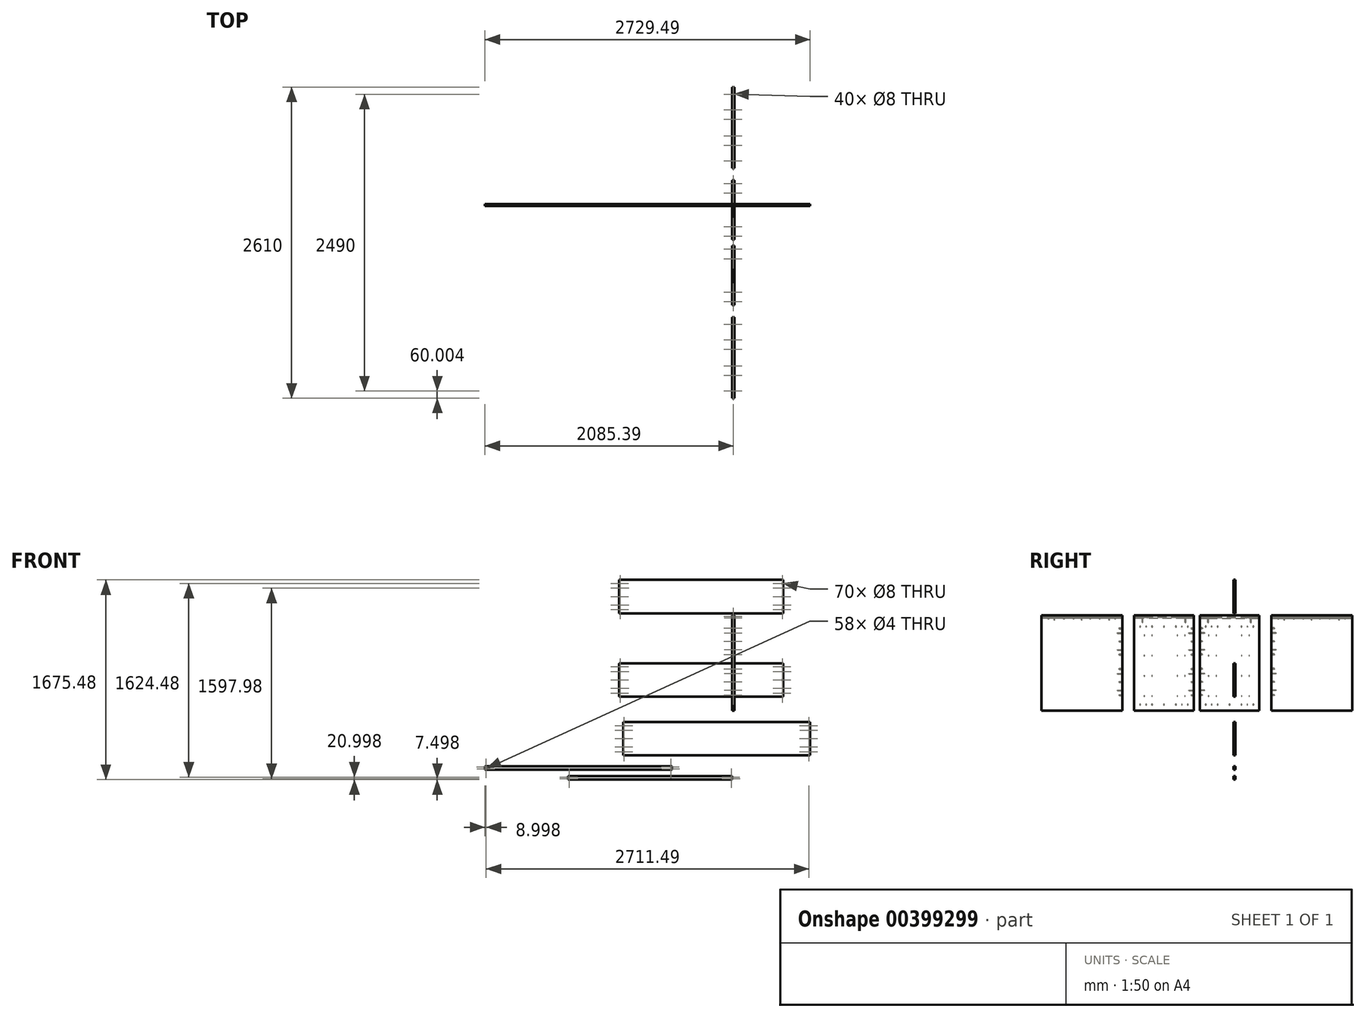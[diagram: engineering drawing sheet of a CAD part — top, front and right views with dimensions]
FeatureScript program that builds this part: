
annotation { "Feature Type Name" : "Feature", "Feature Type Description" : "" }
export const myFeature = defineFeature(function(context is Context, id is Id, definition is map)
    precondition{}
    {
        {
            var Q0;
            Q0=qCreatedBy(makeId("Right.planeOp"),FACE);
            var sketch = newSketch(context, id + "F0", { "sketchPlane" : qUnion([Q0])});
            skLineSegment(sketch, "E0.bottom", {"start": v(-300.67, 487.5) * mm, "end": v(199.33, 487.5) * mm});
            skLineSegment(sketch, "E0.top", {"start": v(-300.67, -312.5) * mm, "end": v(199.33, -312.5) * mm});
            skLineSegment(sketch, "E0.left", {"start": v(-300.67, 487.5) * mm, "end": v(-300.67, -312.5) * mm});
            skLineSegment(sketch, "E0.right", {"start": v(199.33, 487.5) * mm, "end": v(199.33, -312.5) * mm});
            skSolve(sketch);
        }
        {
            var Q0;
            Q0=makeQuery(id+"F0.imprint","IMPRINT",FACE,{"disambiguationData":[TD([[makeQuery(id+"F0.imprint","IMPRINT",EDGE,{"derivedFrom":sQuery(id+"F0.wireOp",EDGE,"E0.bottom")}),-1.0]])]});
            var sketch = newSketch(context, id + "F1", { "sketchPlane" : qUnion([Q0])});
            skLineSegment(sketch, "E1", {"start": v(-300.67, -262.5) * mm, "end": v(199.33, -262.5) * mm, "construction": true});
            skPoint(sketch, "E2", {"position": v(-250.67, -262.5) * mm});
            skPoint(sketch, "E3.1.0.0", {"position": v(-150.67, -262.5) * mm});
            skPoint(sketch, "E3.2.0.0", {"position": v(-50.67, -262.5) * mm});
            skPoint(sketch, "E3.3.0.0", {"position": v(49.33, -262.5) * mm});
            skPoint(sketch, "E3.4.0.0", {"position": v(149.33, -262.5) * mm});
            skLineSegment(sketch, "E3.direction1", {"start": v(-250.67, -262.5) * mm, "end": v(-150.67, -262.5) * mm, "construction": true});
            skPoint(sketch, "E4", {"position": v(99.33, -262.5) * mm});
            skPoint(sketch, "E5", {"position": v(-200.67, -262.5) * mm});
            skPoint(sketch, "E6.0.1.0", {"position": v(99.33, 392.5) * mm});
            skPoint(sketch, "E6.0.1.1", {"position": v(-150.67, 392.5) * mm});
            skPoint(sketch, "E6.0.1.2", {"position": v(-250.67, 392.5) * mm});
            skLineSegment(sketch, "E6.0.1.3", {"start": v(-300.67, 392.5) * mm, "end": v(199.33, 392.5) * mm, "construction": true});
            skPoint(sketch, "E6.0.1.4", {"position": v(-50.67, 392.5) * mm});
            skPoint(sketch, "E6.0.1.5", {"position": v(149.33, 392.5) * mm});
            skPoint(sketch, "E6.0.1.6", {"position": v(-200.67, 392.5) * mm});
            skPoint(sketch, "E6.0.1.7", {"position": v(49.33, 392.5) * mm});
            skLineSegment(sketch, "E6.0.1.8", {"start": v(-250.67, 392.5) * mm, "end": v(-150.67, 392.5) * mm, "construction": true});
            skPoint(sketch, "E6.1.0.0", {"position": v(124.33, -262.5) * mm});
            skPoint(sketch, "E6.1.0.1", {"position": v(-125.67, -262.5) * mm});
            skPoint(sketch, "E6.1.0.2", {"position": v(-225.67, -262.5) * mm});
            skLineSegment(sketch, "E6.1.0.3", {"start": v(-275.67, -262.5) * mm, "end": v(224.33, -262.5) * mm, "construction": true});
            skPoint(sketch, "E6.1.0.4", {"position": v(-25.67, -262.5) * mm});
            skPoint(sketch, "E6.1.0.5", {"position": v(174.33, -262.5) * mm});
            skPoint(sketch, "E6.1.0.6", {"position": v(-175.67, -262.5) * mm});
            skPoint(sketch, "E6.1.0.7", {"position": v(74.33, -262.5) * mm});
            skLineSegment(sketch, "E6.1.0.8", {"start": v(-225.67, -262.5) * mm, "end": v(-125.67, -262.5) * mm, "construction": true});
            skPoint(sketch, "E6.1.1.0", {"position": v(124.33, 392.5) * mm});
            skPoint(sketch, "E6.1.1.1", {"position": v(-125.67, 392.5) * mm});
            skPoint(sketch, "E6.1.1.2", {"position": v(-225.67, 392.5) * mm});
            skLineSegment(sketch, "E6.1.1.3", {"start": v(-275.67, 392.5) * mm, "end": v(224.33, 392.5) * mm, "construction": true});
            skPoint(sketch, "E6.1.1.4", {"position": v(-25.67, 392.5) * mm});
            skPoint(sketch, "E6.1.1.5", {"position": v(174.33, 392.5) * mm});
            skPoint(sketch, "E6.1.1.6", {"position": v(-175.67, 392.5) * mm});
            skPoint(sketch, "E6.1.1.7", {"position": v(74.33, 392.5) * mm});
            skLineSegment(sketch, "E6.1.1.8", {"start": v(-225.67, 392.5) * mm, "end": v(-125.67, 392.5) * mm, "construction": true});
            skPoint(sketch, "E6.2.0.1", {"position": v(-100.67, -262.5) * mm});
            skLineSegment(sketch, "E6.2.0.3", {"start": v(-250.67, -262.5) * mm, "end": v(249.33, -262.5) * mm, "construction": true});
            skPoint(sketch, "E6.2.0.4", {"position": v(-0.67, -262.5) * mm});
            skPoint(sketch, "E6.2.0.5", {"position": v(199.33, -262.5) * mm});
            skLineSegment(sketch, "E6.2.0.8", {"start": v(-200.67, -262.5) * mm, "end": v(-100.67, -262.5) * mm, "construction": true});
            skPoint(sketch, "E6.2.1.0", {"position": v(149.33, 392.5) * mm});
            skPoint(sketch, "E6.2.1.1", {"position": v(-100.67, 392.5) * mm});
            skPoint(sketch, "E6.2.1.2", {"position": v(-200.67, 392.5) * mm});
            skLineSegment(sketch, "E6.2.1.3", {"start": v(-250.67, 392.5) * mm, "end": v(249.33, 392.5) * mm, "construction": true});
            skPoint(sketch, "E6.2.1.4", {"position": v(-0.67, 392.5) * mm});
            skPoint(sketch, "E6.2.1.5", {"position": v(199.33, 392.5) * mm});
            skPoint(sketch, "E6.2.1.6", {"position": v(-150.67, 392.5) * mm});
            skPoint(sketch, "E6.2.1.7", {"position": v(99.33, 392.5) * mm});
            skLineSegment(sketch, "E6.2.1.8", {"start": v(-200.67, 392.5) * mm, "end": v(-100.67, 392.5) * mm, "construction": true});
            skLineSegment(sketch, "E6.direction1", {"start": v(-300.67, -262.5) * mm, "end": v(-275.67, -262.5) * mm, "construction": true});
            skLineSegment(sketch, "E6.direction2", {"start": v(-300.67, -262.5) * mm, "end": v(-300.67, 392.5) * mm, "construction": true});
            skSolve(sketch);
        }
        {
            var Q0;
            Q0=makeQuery(id+"F0.imprint","IMPRINT",FACE,{"disambiguationData":[TD([[makeQuery(id+"F0.imprint","IMPRINT",EDGE,{"derivedFrom":sQuery(id+"F0.wireOp",EDGE,"E0.bottom")}),-1.0]])]});
            var sketch = newSketch(context, id + "F2", { "sketchPlane" : qUnion([Q0])});
            skLineSegment(sketch, "E7.bottom", {"start": v(-263.67, -174.1) * mm, "end": v(186.33, -174.1) * mm});
            skLineSegment(sketch, "E7.top", {"start": v(-263.67, -208.9) * mm, "end": v(186.33, -208.9) * mm});
            skLineSegment(sketch, "E7.left", {"start": v(-263.67, -174.1) * mm, "end": v(-263.67, -208.9) * mm});
            skLineSegment(sketch, "E7.right", {"start": v(186.33, -174.1) * mm, "end": v(186.33, -208.9) * mm});
            skLineSegment(sketch, "E8", {"start": v(186.33, -191.5) * mm, "end": v(-263.67, -191.5) * mm, "construction": true});
            skCircle(sketch, "E9", {"center": v(114.63, -191.5) * mm, "radius": 2.5 * mm});
            skCircle(sketch, "E10", {"center": v(-226.42, -191.5) * mm, "radius": 2.5 * mm});
            skCircle(sketch, "E11", {"center": v(-162.42, -191.5) * mm, "radius": 2.5 * mm});
            skCircle(sketch, "E12", {"center": v(50.63, -191.5) * mm, "radius": 2.5 * mm});
            skCircle(sketch, "E13", {"center": v(-243.67, -191.5) * mm, "radius": 2.25 * mm});
            skLineSegment(sketch, "E14.bottom", {"start": v(134.63, -189.2) * mm, "end": v(125.23, -189.2) * mm});
            skLineSegment(sketch, "E14.top", {"start": v(134.63, -193.8) * mm, "end": v(125.23, -193.8) * mm});
            skLineSegment(sketch, "E14.left", {"start": v(134.63, -189.2) * mm, "end": v(134.63, -193.8) * mm});
            skLineSegment(sketch, "E14.right", {"start": v(125.23, -189.2) * mm, "end": v(125.23, -193.8) * mm});
            skPoint(sketch, "E14.middle", {"position": v(129.93, -191.5) * mm});
            skLineSegment(sketch, "E15.bottom", {"start": v(159.33, -189.2) * mm, "end": v(149.93, -189.2) * mm});
            skLineSegment(sketch, "E15.top", {"start": v(159.33, -193.8) * mm, "end": v(149.93, -193.8) * mm});
            skLineSegment(sketch, "E15.left", {"start": v(159.33, -189.2) * mm, "end": v(159.33, -193.8) * mm});
            skLineSegment(sketch, "E15.right", {"start": v(149.93, -189.2) * mm, "end": v(149.93, -193.8) * mm});
            skPoint(sketch, "E15.middle", {"position": v(154.63, -191.5) * mm});
            skLineSegment(sketch, "E16.bottom", {"start": v(70.63, -189.2) * mm, "end": v(61.23, -189.2) * mm});
            skLineSegment(sketch, "E16.top", {"start": v(70.63, -193.8) * mm, "end": v(61.23, -193.8) * mm});
            skLineSegment(sketch, "E16.left", {"start": v(70.63, -189.2) * mm, "end": v(70.63, -193.8) * mm});
            skLineSegment(sketch, "E16.right", {"start": v(61.23, -189.2) * mm, "end": v(61.23, -193.8) * mm});
            skPoint(sketch, "E16.middle", {"position": v(65.93, -191.5) * mm});
            skLineSegment(sketch, "E17.bottom", {"start": v(96.43, -189.2) * mm, "end": v(87.03, -189.2) * mm});
            skLineSegment(sketch, "E17.top", {"start": v(96.43, -193.8) * mm, "end": v(87.03, -193.8) * mm});
            skLineSegment(sketch, "E17.left", {"start": v(96.43, -189.2) * mm, "end": v(96.43, -193.8) * mm});
            skLineSegment(sketch, "E17.right", {"start": v(87.03, -189.2) * mm, "end": v(87.03, -193.8) * mm});
            skPoint(sketch, "E17.middle", {"position": v(91.73, -191.5) * mm});
            skLineSegment(sketch, "E18.bottom", {"start": v(-142.42, -189.2) * mm, "end": v(-151.82, -189.2) * mm});
            skLineSegment(sketch, "E18.top", {"start": v(-142.42, -193.8) * mm, "end": v(-151.82, -193.8) * mm});
            skLineSegment(sketch, "E18.left", {"start": v(-142.42, -189.2) * mm, "end": v(-142.42, -193.8) * mm});
            skLineSegment(sketch, "E18.right", {"start": v(-151.82, -189.2) * mm, "end": v(-151.82, -193.8) * mm});
            skPoint(sketch, "E18.middle", {"position": v(-147.12, -191.5) * mm});
            skLineSegment(sketch, "E19.bottom", {"start": v(-117.72, -189.2) * mm, "end": v(-127.12, -189.2) * mm});
            skLineSegment(sketch, "E19.top", {"start": v(-117.72, -193.8) * mm, "end": v(-127.12, -193.8) * mm});
            skLineSegment(sketch, "E19.left", {"start": v(-117.72, -189.2) * mm, "end": v(-117.72, -193.8) * mm});
            skLineSegment(sketch, "E19.right", {"start": v(-127.12, -189.2) * mm, "end": v(-127.12, -193.8) * mm});
            skPoint(sketch, "E19.middle", {"position": v(-122.42, -191.5) * mm});
            skLineSegment(sketch, "E20.bottom", {"start": v(-206.42, -189.2) * mm, "end": v(-215.82, -189.2) * mm});
            skLineSegment(sketch, "E20.top", {"start": v(-206.42, -193.8) * mm, "end": v(-215.82, -193.8) * mm});
            skLineSegment(sketch, "E20.left", {"start": v(-206.42, -189.2) * mm, "end": v(-206.42, -193.8) * mm});
            skLineSegment(sketch, "E20.right", {"start": v(-215.82, -189.2) * mm, "end": v(-215.82, -193.8) * mm});
            skPoint(sketch, "E20.middle", {"position": v(-211.12, -191.5) * mm});
            skLineSegment(sketch, "E21.bottom", {"start": v(-180.62, -189.2) * mm, "end": v(-190.02, -189.2) * mm});
            skLineSegment(sketch, "E21.top", {"start": v(-180.62, -193.8) * mm, "end": v(-190.02, -193.8) * mm});
            skLineSegment(sketch, "E21.left", {"start": v(-180.62, -189.2) * mm, "end": v(-180.62, -193.8) * mm});
            skLineSegment(sketch, "E21.right", {"start": v(-190.02, -189.2) * mm, "end": v(-190.02, -193.8) * mm});
            skPoint(sketch, "E21.middle", {"position": v(-185.32, -191.5) * mm});
            skLineSegment(sketch, "E22.0.1.0", {"start": v(186.33, -4.1) * mm, "end": v(186.33, -38.9) * mm});
            skPoint(sketch, "E22.0.1.1", {"position": v(-147.12, -21.5) * mm});
            skPoint(sketch, "E22.0.1.2", {"position": v(91.73, -21.5) * mm});
            skLineSegment(sketch, "E22.0.1.3", {"start": v(186.33, -21.5) * mm, "end": v(-263.67, -21.5) * mm, "construction": true});
            skPoint(sketch, "E22.0.1.4", {"position": v(-211.12, -21.5) * mm});
            skPoint(sketch, "E22.0.1.5", {"position": v(-185.32, -21.5) * mm});
            skLineSegment(sketch, "E22.0.1.6", {"start": v(-263.67, -4.1) * mm, "end": v(-263.67, -38.9) * mm});
            skLineSegment(sketch, "E22.0.1.7", {"start": v(-263.67, -4.1) * mm, "end": v(186.33, -4.1) * mm});
            skPoint(sketch, "E22.0.1.8", {"position": v(-122.42, -21.5) * mm});
            skPoint(sketch, "E22.0.1.9", {"position": v(154.63, -21.5) * mm});
            skPoint(sketch, "E22.0.1.10", {"position": v(129.93, -21.5) * mm});
            skLineSegment(sketch, "E22.0.1.11", {"start": v(-263.67, -38.9) * mm, "end": v(186.33, -38.9) * mm});
            skPoint(sketch, "E22.0.1.12", {"position": v(65.93, -21.5) * mm});
            skCircle(sketch, "E22.0.1.13", {"center": v(114.63, -21.5) * mm, "radius": 2.5 * mm});
            skCircle(sketch, "E22.0.1.14", {"center": v(-162.42, -21.5) * mm, "radius": 2.5 * mm});
            skCircle(sketch, "E22.0.1.15", {"center": v(-243.67, -21.5) * mm, "radius": 2.25 * mm});
            skCircle(sketch, "E22.0.1.16", {"center": v(-226.42, -21.5) * mm, "radius": 2.5 * mm});
            skCircle(sketch, "E22.0.1.17", {"center": v(50.63, -21.5) * mm, "radius": 2.5 * mm});
            skLineSegment(sketch, "E22.0.1.18", {"start": v(96.43, -19.2) * mm, "end": v(96.43, -23.8) * mm});
            skLineSegment(sketch, "E22.0.1.19", {"start": v(159.33, -19.2) * mm, "end": v(159.33, -23.8) * mm});
            skLineSegment(sketch, "E22.0.1.20", {"start": v(96.43, -23.8) * mm, "end": v(87.03, -23.8) * mm});
            skLineSegment(sketch, "E22.0.1.21", {"start": v(-180.62, -19.2) * mm, "end": v(-180.62, -23.8) * mm});
            skLineSegment(sketch, "E22.0.1.22", {"start": v(-117.72, -19.2) * mm, "end": v(-117.72, -23.8) * mm});
            skLineSegment(sketch, "E22.0.1.23", {"start": v(134.63, -23.8) * mm, "end": v(125.23, -23.8) * mm});
            skLineSegment(sketch, "E22.0.1.24", {"start": v(134.63, -19.2) * mm, "end": v(125.23, -19.2) * mm});
            skLineSegment(sketch, "E22.0.1.25", {"start": v(87.03, -19.2) * mm, "end": v(87.03, -23.8) * mm});
            skLineSegment(sketch, "E22.0.1.26", {"start": v(149.93, -19.2) * mm, "end": v(149.93, -23.8) * mm});
            skLineSegment(sketch, "E22.0.1.27", {"start": v(125.23, -19.2) * mm, "end": v(125.23, -23.8) * mm});
            skLineSegment(sketch, "E22.0.1.28", {"start": v(96.43, -19.2) * mm, "end": v(87.03, -19.2) * mm});
            skLineSegment(sketch, "E22.0.1.29", {"start": v(159.33, -23.8) * mm, "end": v(149.93, -23.8) * mm});
            skLineSegment(sketch, "E22.0.1.30", {"start": v(-190.02, -19.2) * mm, "end": v(-190.02, -23.8) * mm});
            skLineSegment(sketch, "E22.0.1.31", {"start": v(-180.62, -23.8) * mm, "end": v(-190.02, -23.8) * mm});
            skLineSegment(sketch, "E22.0.1.32", {"start": v(-151.82, -19.2) * mm, "end": v(-151.82, -23.8) * mm});
            skLineSegment(sketch, "E22.0.1.33", {"start": v(-180.62, -19.2) * mm, "end": v(-190.02, -19.2) * mm});
            skLineSegment(sketch, "E22.0.1.34", {"start": v(159.33, -19.2) * mm, "end": v(149.93, -19.2) * mm});
            skLineSegment(sketch, "E22.0.1.35", {"start": v(134.63, -19.2) * mm, "end": v(134.63, -23.8) * mm});
            skLineSegment(sketch, "E22.0.1.36", {"start": v(-142.42, -23.8) * mm, "end": v(-151.82, -23.8) * mm});
            skLineSegment(sketch, "E22.0.1.37", {"start": v(70.63, -19.2) * mm, "end": v(70.63, -23.8) * mm});
            skLineSegment(sketch, "E22.0.1.38", {"start": v(-142.42, -19.2) * mm, "end": v(-151.82, -19.2) * mm});
            skLineSegment(sketch, "E22.0.1.39", {"start": v(-117.72, -23.8) * mm, "end": v(-127.12, -23.8) * mm});
            skLineSegment(sketch, "E22.0.1.40", {"start": v(70.63, -23.8) * mm, "end": v(61.23, -23.8) * mm});
            skLineSegment(sketch, "E22.0.1.41", {"start": v(-127.12, -19.2) * mm, "end": v(-127.12, -23.8) * mm});
            skLineSegment(sketch, "E22.0.1.42", {"start": v(-117.72, -19.2) * mm, "end": v(-127.12, -19.2) * mm});
            skLineSegment(sketch, "E22.0.1.43", {"start": v(-206.42, -23.8) * mm, "end": v(-215.82, -23.8) * mm});
            skLineSegment(sketch, "E22.0.1.44", {"start": v(70.63, -19.2) * mm, "end": v(61.23, -19.2) * mm});
            skLineSegment(sketch, "E22.0.1.45", {"start": v(61.23, -19.2) * mm, "end": v(61.23, -23.8) * mm});
            skLineSegment(sketch, "E22.0.1.46", {"start": v(-206.42, -19.2) * mm, "end": v(-215.82, -19.2) * mm});
            skLineSegment(sketch, "E22.0.1.47", {"start": v(-215.82, -19.2) * mm, "end": v(-215.82, -23.8) * mm});
            skLineSegment(sketch, "E22.0.1.48", {"start": v(-206.42, -19.2) * mm, "end": v(-206.42, -23.8) * mm});
            skLineSegment(sketch, "E22.0.1.49", {"start": v(-142.42, -19.2) * mm, "end": v(-142.42, -23.8) * mm});
            skLineSegment(sketch, "E22.0.2.0", {"start": v(186.33, 165.9) * mm, "end": v(186.33, 131.1) * mm});
            skPoint(sketch, "E22.0.2.1", {"position": v(-147.12, 148.5) * mm});
            skPoint(sketch, "E22.0.2.2", {"position": v(91.73, 148.5) * mm});
            skLineSegment(sketch, "E22.0.2.3", {"start": v(186.33, 148.5) * mm, "end": v(-263.67, 148.5) * mm, "construction": true});
            skPoint(sketch, "E22.0.2.4", {"position": v(-211.12, 148.5) * mm});
            skPoint(sketch, "E22.0.2.5", {"position": v(-185.32, 148.5) * mm});
            skLineSegment(sketch, "E22.0.2.6", {"start": v(-263.67, 165.9) * mm, "end": v(-263.67, 131.1) * mm});
            skLineSegment(sketch, "E22.0.2.7", {"start": v(-263.67, 165.9) * mm, "end": v(186.33, 165.9) * mm});
            skPoint(sketch, "E22.0.2.8", {"position": v(-122.42, 148.5) * mm});
            skPoint(sketch, "E22.0.2.9", {"position": v(154.63, 148.5) * mm});
            skPoint(sketch, "E22.0.2.10", {"position": v(129.93, 148.5) * mm});
            skLineSegment(sketch, "E22.0.2.11", {"start": v(-263.67, 131.1) * mm, "end": v(186.33, 131.1) * mm});
            skPoint(sketch, "E22.0.2.12", {"position": v(65.93, 148.5) * mm});
            skCircle(sketch, "E22.0.2.13", {"center": v(114.63, 148.5) * mm, "radius": 2.5 * mm});
            skCircle(sketch, "E22.0.2.14", {"center": v(-162.42, 148.5) * mm, "radius": 2.5 * mm});
            skCircle(sketch, "E22.0.2.15", {"center": v(-243.67, 148.5) * mm, "radius": 2.25 * mm});
            skCircle(sketch, "E22.0.2.16", {"center": v(-226.42, 148.5) * mm, "radius": 2.5 * mm});
            skCircle(sketch, "E22.0.2.17", {"center": v(50.63, 148.5) * mm, "radius": 2.5 * mm});
            skLineSegment(sketch, "E22.0.2.18", {"start": v(96.43, 150.8) * mm, "end": v(96.43, 146.2) * mm});
            skLineSegment(sketch, "E22.0.2.19", {"start": v(159.33, 150.8) * mm, "end": v(159.33, 146.2) * mm});
            skLineSegment(sketch, "E22.0.2.20", {"start": v(96.43, 146.2) * mm, "end": v(87.03, 146.2) * mm});
            skLineSegment(sketch, "E22.0.2.21", {"start": v(-180.62, 150.8) * mm, "end": v(-180.62, 146.2) * mm});
            skLineSegment(sketch, "E22.0.2.22", {"start": v(-117.72, 150.8) * mm, "end": v(-117.72, 146.2) * mm});
            skLineSegment(sketch, "E22.0.2.23", {"start": v(134.63, 146.2) * mm, "end": v(125.23, 146.2) * mm});
            skLineSegment(sketch, "E22.0.2.24", {"start": v(134.63, 150.8) * mm, "end": v(125.23, 150.8) * mm});
            skLineSegment(sketch, "E22.0.2.25", {"start": v(87.03, 150.8) * mm, "end": v(87.03, 146.2) * mm});
            skLineSegment(sketch, "E22.0.2.26", {"start": v(149.93, 150.8) * mm, "end": v(149.93, 146.2) * mm});
            skLineSegment(sketch, "E22.0.2.27", {"start": v(125.23, 150.8) * mm, "end": v(125.23, 146.2) * mm});
            skLineSegment(sketch, "E22.0.2.28", {"start": v(96.43, 150.8) * mm, "end": v(87.03, 150.8) * mm});
            skLineSegment(sketch, "E22.0.2.29", {"start": v(159.33, 146.2) * mm, "end": v(149.93, 146.2) * mm});
            skLineSegment(sketch, "E22.0.2.30", {"start": v(-190.02, 150.8) * mm, "end": v(-190.02, 146.2) * mm});
            skLineSegment(sketch, "E22.0.2.31", {"start": v(-180.62, 146.2) * mm, "end": v(-190.02, 146.2) * mm});
            skLineSegment(sketch, "E22.0.2.32", {"start": v(-151.82, 150.8) * mm, "end": v(-151.82, 146.2) * mm});
            skLineSegment(sketch, "E22.0.2.33", {"start": v(-180.62, 150.8) * mm, "end": v(-190.02, 150.8) * mm});
            skLineSegment(sketch, "E22.0.2.34", {"start": v(159.33, 150.8) * mm, "end": v(149.93, 150.8) * mm});
            skLineSegment(sketch, "E22.0.2.35", {"start": v(134.63, 150.8) * mm, "end": v(134.63, 146.2) * mm});
            skLineSegment(sketch, "E22.0.2.36", {"start": v(-142.42, 146.2) * mm, "end": v(-151.82, 146.2) * mm});
            skLineSegment(sketch, "E22.0.2.37", {"start": v(70.63, 150.8) * mm, "end": v(70.63, 146.2) * mm});
            skLineSegment(sketch, "E22.0.2.38", {"start": v(-142.42, 150.8) * mm, "end": v(-151.82, 150.8) * mm});
            skLineSegment(sketch, "E22.0.2.39", {"start": v(-117.72, 146.2) * mm, "end": v(-127.12, 146.2) * mm});
            skLineSegment(sketch, "E22.0.2.40", {"start": v(70.63, 146.2) * mm, "end": v(61.23, 146.2) * mm});
            skLineSegment(sketch, "E22.0.2.41", {"start": v(-127.12, 150.8) * mm, "end": v(-127.12, 146.2) * mm});
            skLineSegment(sketch, "E22.0.2.42", {"start": v(-117.72, 150.8) * mm, "end": v(-127.12, 150.8) * mm});
            skLineSegment(sketch, "E22.0.2.43", {"start": v(-206.42, 146.2) * mm, "end": v(-215.82, 146.2) * mm});
            skLineSegment(sketch, "E22.0.2.44", {"start": v(70.63, 150.8) * mm, "end": v(61.23, 150.8) * mm});
            skLineSegment(sketch, "E22.0.2.45", {"start": v(61.23, 150.8) * mm, "end": v(61.23, 146.2) * mm});
            skLineSegment(sketch, "E22.0.2.46", {"start": v(-206.42, 150.8) * mm, "end": v(-215.82, 150.8) * mm});
            skLineSegment(sketch, "E22.0.2.47", {"start": v(-215.82, 150.8) * mm, "end": v(-215.82, 146.2) * mm});
            skLineSegment(sketch, "E22.0.2.48", {"start": v(-206.42, 150.8) * mm, "end": v(-206.42, 146.2) * mm});
            skLineSegment(sketch, "E22.0.2.49", {"start": v(-142.42, 150.8) * mm, "end": v(-142.42, 146.2) * mm});
            skLineSegment(sketch, "E22.0.3.0", {"start": v(186.33, 335.9) * mm, "end": v(186.33, 301.1) * mm});
            skPoint(sketch, "E22.0.3.1", {"position": v(-147.12, 318.5) * mm});
            skPoint(sketch, "E22.0.3.2", {"position": v(91.73, 318.5) * mm});
            skLineSegment(sketch, "E22.0.3.3", {"start": v(186.33, 318.5) * mm, "end": v(-263.67, 318.5) * mm, "construction": true});
            skPoint(sketch, "E22.0.3.4", {"position": v(-211.12, 318.5) * mm});
            skPoint(sketch, "E22.0.3.5", {"position": v(-185.32, 318.5) * mm});
            skLineSegment(sketch, "E22.0.3.6", {"start": v(-263.67, 335.9) * mm, "end": v(-263.67, 301.1) * mm});
            skLineSegment(sketch, "E22.0.3.7", {"start": v(-263.67, 335.9) * mm, "end": v(186.33, 335.9) * mm});
            skPoint(sketch, "E22.0.3.8", {"position": v(-122.42, 318.5) * mm});
            skPoint(sketch, "E22.0.3.9", {"position": v(154.63, 318.5) * mm});
            skPoint(sketch, "E22.0.3.10", {"position": v(129.93, 318.5) * mm});
            skLineSegment(sketch, "E22.0.3.11", {"start": v(-263.67, 301.1) * mm, "end": v(186.33, 301.1) * mm});
            skPoint(sketch, "E22.0.3.12", {"position": v(65.93, 318.5) * mm});
            skCircle(sketch, "E22.0.3.13", {"center": v(114.63, 318.5) * mm, "radius": 2.5 * mm});
            skCircle(sketch, "E22.0.3.14", {"center": v(-162.42, 318.5) * mm, "radius": 2.5 * mm});
            skCircle(sketch, "E22.0.3.15", {"center": v(-243.67, 318.5) * mm, "radius": 2.25 * mm});
            skCircle(sketch, "E22.0.3.16", {"center": v(-226.42, 318.5) * mm, "radius": 2.5 * mm});
            skCircle(sketch, "E22.0.3.17", {"center": v(50.63, 318.5) * mm, "radius": 2.5 * mm});
            skLineSegment(sketch, "E22.0.3.18", {"start": v(96.43, 320.8) * mm, "end": v(96.43, 316.2) * mm});
            skLineSegment(sketch, "E22.0.3.19", {"start": v(159.33, 320.8) * mm, "end": v(159.33, 316.2) * mm});
            skLineSegment(sketch, "E22.0.3.20", {"start": v(96.43, 316.2) * mm, "end": v(87.03, 316.2) * mm});
            skLineSegment(sketch, "E22.0.3.21", {"start": v(-180.62, 320.8) * mm, "end": v(-180.62, 316.2) * mm});
            skLineSegment(sketch, "E22.0.3.22", {"start": v(-117.72, 320.8) * mm, "end": v(-117.72, 316.2) * mm});
            skLineSegment(sketch, "E22.0.3.23", {"start": v(134.63, 316.2) * mm, "end": v(125.23, 316.2) * mm});
            skLineSegment(sketch, "E22.0.3.24", {"start": v(134.63, 320.8) * mm, "end": v(125.23, 320.8) * mm});
            skLineSegment(sketch, "E22.0.3.25", {"start": v(87.03, 320.8) * mm, "end": v(87.03, 316.2) * mm});
            skLineSegment(sketch, "E22.0.3.26", {"start": v(149.93, 320.8) * mm, "end": v(149.93, 316.2) * mm});
            skLineSegment(sketch, "E22.0.3.27", {"start": v(125.23, 320.8) * mm, "end": v(125.23, 316.2) * mm});
            skLineSegment(sketch, "E22.0.3.28", {"start": v(96.43, 320.8) * mm, "end": v(87.03, 320.8) * mm});
            skLineSegment(sketch, "E22.0.3.29", {"start": v(159.33, 316.2) * mm, "end": v(149.93, 316.2) * mm});
            skLineSegment(sketch, "E22.0.3.30", {"start": v(-190.02, 320.8) * mm, "end": v(-190.02, 316.2) * mm});
            skLineSegment(sketch, "E22.0.3.31", {"start": v(-180.62, 316.2) * mm, "end": v(-190.02, 316.2) * mm});
            skLineSegment(sketch, "E22.0.3.32", {"start": v(-151.82, 320.8) * mm, "end": v(-151.82, 316.2) * mm});
            skLineSegment(sketch, "E22.0.3.33", {"start": v(-180.62, 320.8) * mm, "end": v(-190.02, 320.8) * mm});
            skLineSegment(sketch, "E22.0.3.34", {"start": v(159.33, 320.8) * mm, "end": v(149.93, 320.8) * mm});
            skLineSegment(sketch, "E22.0.3.35", {"start": v(134.63, 320.8) * mm, "end": v(134.63, 316.2) * mm});
            skLineSegment(sketch, "E22.0.3.36", {"start": v(-142.42, 316.2) * mm, "end": v(-151.82, 316.2) * mm});
            skLineSegment(sketch, "E22.0.3.37", {"start": v(70.63, 320.8) * mm, "end": v(70.63, 316.2) * mm});
            skLineSegment(sketch, "E22.0.3.38", {"start": v(-142.42, 320.8) * mm, "end": v(-151.82, 320.8) * mm});
            skLineSegment(sketch, "E22.0.3.39", {"start": v(-117.72, 316.2) * mm, "end": v(-127.12, 316.2) * mm});
            skLineSegment(sketch, "E22.0.3.40", {"start": v(70.63, 316.2) * mm, "end": v(61.23, 316.2) * mm});
            skLineSegment(sketch, "E22.0.3.41", {"start": v(-127.12, 320.8) * mm, "end": v(-127.12, 316.2) * mm});
            skLineSegment(sketch, "E22.0.3.42", {"start": v(-117.72, 320.8) * mm, "end": v(-127.12, 320.8) * mm});
            skLineSegment(sketch, "E22.0.3.43", {"start": v(-206.42, 316.2) * mm, "end": v(-215.82, 316.2) * mm});
            skLineSegment(sketch, "E22.0.3.44", {"start": v(70.63, 320.8) * mm, "end": v(61.23, 320.8) * mm});
            skLineSegment(sketch, "E22.0.3.45", {"start": v(61.23, 320.8) * mm, "end": v(61.23, 316.2) * mm});
            skLineSegment(sketch, "E22.0.3.46", {"start": v(-206.42, 320.8) * mm, "end": v(-215.82, 320.8) * mm});
            skLineSegment(sketch, "E22.0.3.47", {"start": v(-215.82, 320.8) * mm, "end": v(-215.82, 316.2) * mm});
            skLineSegment(sketch, "E22.0.3.48", {"start": v(-206.42, 320.8) * mm, "end": v(-206.42, 316.2) * mm});
            skLineSegment(sketch, "E22.0.3.49", {"start": v(-142.42, 320.8) * mm, "end": v(-142.42, 316.2) * mm});
            skLineSegment(sketch, "E22.direction1", {"start": v(-263.67, -208.9) * mm, "end": v(-238.67, -208.9) * mm, "construction": true});
            skLineSegment(sketch, "E22.direction2", {"start": v(-263.67, -208.9) * mm, "end": v(-263.67, -38.9) * mm, "construction": true});
            skSolve(sketch);
        }
        {
            var Q0;
            Q0=qSketchRegion(id+"F0",true);
            extrude(context, id + "F3", {"entities" : qUnion([Q0]), "depth" : 18 * mm});
        }
        {
            var Q0;
            Q0=sQuery(id+"F2.wireOp",VERTEX,"E9.center");
            var Q1;
            Q1=sQuery(id+"F2.wireOp",VERTEX,"E12.center");
            var Q2;
            Q2=sQuery(id+"F2.wireOp",VERTEX,"E11.center");
            var Q3;
            Q3=sQuery(id+"F2.wireOp",VERTEX,"E10.center");
            var Q4;
            Q4=sQuery(id+"F2.wireOp",VERTEX,"E22.0.1.13.center");
            var Q5;
            Q5=sQuery(id+"F2.wireOp",VERTEX,"E22.0.1.17.center");
            var Q6;
            Q6=sQuery(id+"F2.wireOp",VERTEX,"E22.0.1.14.center");
            var Q7;
            Q7=sQuery(id+"F2.wireOp",VERTEX,"E22.0.1.16.center");
            var Q8;
            Q8=sQuery(id+"F2.wireOp",VERTEX,"E22.0.3.16.center");
            var Q9;
            Q9=sQuery(id+"F2.wireOp",VERTEX,"E22.0.2.16.center");
            var Q10;
            Q10=sQuery(id+"F2.wireOp",VERTEX,"E22.0.2.14.center");
            var Q11;
            Q11=sQuery(id+"F2.wireOp",VERTEX,"E22.0.3.14.center");
            var Q12;
            Q12=sQuery(id+"F2.wireOp",VERTEX,"E22.0.3.13.center");
            var Q13;
            Q13=sQuery(id+"F2.wireOp",VERTEX,"E22.0.2.13.center");
            var Q14;
            Q14=sQuery(id+"F2.wireOp",VERTEX,"E22.0.2.17.center");
            var Q15;
            Q15=sQuery(id+"F2.wireOp",VERTEX,"E22.0.3.17.center");
            var Q16;
            Q16=makeQuery(id+"F3.opExtrude","SWEPT_BODY",BODY,{"disambiguationData":[OSD([sQuery(id+"F0.wireOp",EDGE,"E0.bottom"),sQuery(id+"F0.wireOp",EDGE,"E0.top"),sQuery(id+"F0.wireOp",EDGE,"E0.left"),sQuery(id+"F0.wireOp",EDGE,"E0.right")])]});
            hole(context, id + "F4", {"style" : HoleStyle.SIMPLE, "endStyle" : HoleEndStyle.BLIND, "oppositeDirection" : true, "holeDiameter" : 4.5 * mm, "holeDepth" : 10 * mm, "isTappedThrough" : true, "tappedDepth" : 12 * mm, "tapClearance" : 3, "startFromSketch" : true, "locations" : qUnion([Q0, Q1, Q2, Q3, Q4, Q5, Q6, Q7, Q8, Q9, Q10, Q11, Q12, Q13, Q14, Q15]), "scope" : qUnion([Q16])});
        }
        {
            var Q0;
            Q0=sQuery(id+"F1.wireOp",VERTEX,"E2");
            var Q1;
            Q1=sQuery(id+"F1.wireOp",VERTEX,"E3.1.0.0");
            var Q2;
            Q2=sQuery(id+"F1.wireOp",VERTEX,"E3.2.0.0");
            var Q3;
            Q3=sQuery(id+"F1.wireOp",VERTEX,"E3.3.0.0");
            var Q4;
            Q4=sQuery(id+"F1.wireOp",VERTEX,"E3.4.0.0");
            var Q5;
            Q5=sQuery(id+"F1.wireOp",VERTEX,"E6.2.1.0");
            var Q6;
            Q6=sQuery(id+"F1.wireOp",VERTEX,"E6.0.1.7");
            var Q7;
            Q7=sQuery(id+"F1.wireOp",VERTEX,"E6.0.1.4");
            var Q8;
            Q8=sQuery(id+"F1.wireOp",VERTEX,"E6.0.1.2");
            var Q9;
            Q9=sQuery(id+"F1.wireOp",VERTEX,"E6.2.1.6");
            var Q10;
            Q10=makeQuery(id+"F3.opExtrude","SWEPT_BODY",BODY,{"disambiguationData":[OSD([sQuery(id+"F0.wireOp",EDGE,"E0.bottom"),sQuery(id+"F0.wireOp",EDGE,"E0.top"),sQuery(id+"F0.wireOp",EDGE,"E0.left"),sQuery(id+"F0.wireOp",EDGE,"E0.right")])]});
            hole(context, id + "F5", {"style" : HoleStyle.SIMPLE, "endStyle" : HoleEndStyle.BLIND, "oppositeDirection" : true, "holeDiameter" : 8 * mm, "holeDepth" : 10 * mm, "isTappedThrough" : true, "tappedDepth" : 12 * mm, "tapClearance" : 3, "startFromSketch" : true, "locations" : qUnion([Q0, Q1, Q2, Q3, Q4, Q5, Q6, Q7, Q8, Q9]), "scope" : qUnion([Q10])});
        }
        {
            var Q0;
            Q0=sQuery(id+"F1.wireOp",VERTEX,"E4");
            var Q1;
            Q1=sQuery(id+"F1.wireOp",VERTEX,"E5");
            var Q2;
            Q2=sQuery(id+"F1.wireOp",VERTEX,"E6.0.1.0");
            var Q3;
            Q3=sQuery(id+"F1.wireOp",VERTEX,"E6.2.1.2");
            var Q4;
            Q4=makeQuery(id+"F3.opExtrude","SWEPT_BODY",BODY,{"disambiguationData":[OSD([sQuery(id+"F0.wireOp",EDGE,"E0.bottom"),sQuery(id+"F0.wireOp",EDGE,"E0.top"),sQuery(id+"F0.wireOp",EDGE,"E0.left"),sQuery(id+"F0.wireOp",EDGE,"E0.right")])]});
            hole(context, id + "F6", {"style" : HoleStyle.SIMPLE, "endStyle" : HoleEndStyle.BLIND, "oppositeDirection" : true, "holeDiameter" : 5 * mm, "holeDepth" : 10 * mm, "isTappedThrough" : true, "tappedDepth" : 12 * mm, "tapClearance" : 3, "startFromSketch" : true, "locations" : qUnion([Q0, Q1, Q2, Q3]), "scope" : qUnion([Q4])});
        }
        {
            var Q0;
            Q0=qCreatedBy(makeId("Right.planeOp"),FACE);
            var sketch = newSketch(context, id + "F7", { "sketchPlane" : qUnion([Q0])});
            skLineSegment(sketch, "E23.bottom", {"start": v(979.33, 487.5) * mm, "end": v(299.33, 487.5) * mm});
            skLineSegment(sketch, "E23.top", {"start": v(979.33, -312.5) * mm, "end": v(299.33, -312.5) * mm});
            skLineSegment(sketch, "E23.left", {"start": v(979.33, 487.5) * mm, "end": v(979.33, -312.5) * mm});
            skLineSegment(sketch, "E23.right", {"start": v(299.33, 487.5) * mm, "end": v(299.33, -312.5) * mm});
            skLineSegment(sketch, "E24", {"start": v(299.33, -312.5) * mm, "end": v(199.33, -312.5) * mm, "construction": true});
            skSolve(sketch);
        }
        {
            var Q0;
            Q0=makeQuery(id+"F7.imprint","IMPRINT",FACE,{"disambiguationData":[TD([[makeQuery(id+"F7.imprint","IMPRINT",EDGE,{"derivedFrom":sQuery(id+"F7.wireOp",EDGE,"E23.bottom")}),1.0]])]});
            extrude(context, id + "F8", {"entities" : qUnion([Q0]), "depth" : 18 * mm});
        }
        {
            var Q0;
            Q0=makeQuery(id+"F8.opExtrude","SWEPT_FACE",FACE,{"disambiguationData":[OSD([sQuery(id+"F7.wireOp",EDGE,"E23.left")])]});
            var sketch = newSketch(context, id + "F9", { "sketchPlane" : qUnion([Q0])});
            skLineSegment(sketch, "E25", {"start": v(-9, 487.5) * mm, "end": v(-9, 442.5) * mm, "construction": true});
            skPoint(sketch, "E26", {"position": v(-9, 478.5) * mm});
            skPoint(sketch, "E27", {"position": v(-9, 465) * mm});
            skSolve(sketch);
        }
        {
            var Q0;
            Q0=sQuery(id+"F9.wireOp",VERTEX,"E27");
            var Q1;
            Q1=makeQuery(id+"F8.opExtrude","SWEPT_BODY",BODY,{"disambiguationData":[OSD([sQuery(id+"F7.wireOp",EDGE,"E23.bottom"),sQuery(id+"F7.wireOp",EDGE,"E23.top"),sQuery(id+"F7.wireOp",EDGE,"E23.left"),sQuery(id+"F7.wireOp",EDGE,"E23.right")])]});
            hole(context, id + "F10", {"style" : HoleStyle.SIMPLE, "endStyle" : HoleEndStyle.THROUGH, "holeDiameter" : 4 * mm, "isTappedThrough" : true, "tappedDepth" : 12 * mm, "tapClearance" : 3, "locations" : qUnion([Q0]), "scope" : qUnion([Q1])});
        }
        {
            var Q0;
            Q0=sQuery(id+"F9.wireOp",VERTEX,"E26");
            var Q1;
            Q1=makeQuery(id+"F8.opExtrude","SWEPT_BODY",BODY,{"disambiguationData":[OSD([sQuery(id+"F7.wireOp",EDGE,"E23.bottom"),sQuery(id+"F7.wireOp",EDGE,"E23.top"),sQuery(id+"F7.wireOp",EDGE,"E23.left"),sQuery(id+"F7.wireOp",EDGE,"E23.right")])]});
            hole(context, id + "F11", {"style" : HoleStyle.SIMPLE, "endStyle" : HoleEndStyle.THROUGH, "holeDiameter" : 8 * mm, "isTappedThrough" : true, "tappedDepth" : 12 * mm, "tapClearance" : 3, "locations" : qUnion([Q0]), "scope" : qUnion([Q1])});
        }
        {
            var Q0;
            Q0=qCreatedBy(makeId("Front.planeOp"),FACE);
            var sketch = newSketch(context, id + "F12", { "sketchPlane" : qUnion([Q0])});
            skLineSegment(sketch, "E28.bottom", {"start": v(-916.9, -408.71) * mm, "end": v(653.1, -408.71) * mm});
            skLineSegment(sketch, "E28.top", {"start": v(-916.9, -688.71) * mm, "end": v(653.1, -688.71) * mm});
            skLineSegment(sketch, "E28.left", {"start": v(-916.9, -408.71) * mm, "end": v(-916.9, -688.71) * mm});
            skLineSegment(sketch, "E28.right", {"start": v(653.1, -408.71) * mm, "end": v(653.1, -688.71) * mm});
            skSolve(sketch);
        }
        {
            var Q0;
            Q0=qSketchRegion(id+"F12",true);
            extrude(context, id + "F13", {"entities" : qUnion([Q0]), "operationType" : NewBodyOperationType.ADD, "depth" : 18 * mm});
        }
        {
            var Q0;
            Q0=qCreatedBy(makeId("Front.planeOp"),FACE);
            var sketch = newSketch(context, id + "F14", { "sketchPlane" : qUnion([Q0])});
            skLineSegment(sketch, "E29.0.0", {"start": v(-916.9, -408.71) * mm, "end": v(-916.9, -688.71) * mm});
            skLineSegment(sketch, "E29.0.1", {"start": v(-916.9, -688.71) * mm, "end": v(653.1, -688.71) * mm});
            skLineSegment(sketch, "E29.0.2", {"start": v(653.1, -688.71) * mm, "end": v(653.1, -408.71) * mm});
            skLineSegment(sketch, "E29.0.3", {"start": v(653.1, -408.71) * mm, "end": v(-916.9, -408.71) * mm});
            skLineSegment(sketch, "E30.bottom", {"start": v(-951.53, 83.9) * mm, "end": v(428.47, 83.9) * mm});
            skLineSegment(sketch, "E30.top", {"start": v(-951.53, -196.1) * mm, "end": v(428.47, -196.1) * mm});
            skLineSegment(sketch, "E30.left", {"start": v(-951.53, 83.9) * mm, "end": v(-951.53, -196.1) * mm});
            skLineSegment(sketch, "E30.right", {"start": v(428.47, 83.9) * mm, "end": v(428.47, -196.1) * mm});
            skSolve(sketch);
        }
        {
            var Q0;
            Q0=qSketchRegion(id+"F14",true);
            extrude(context, id + "F15", {"entities" : qUnion([Q0]), "depth" : 18 * mm});
        }
        {
            var Q0;
            Q0=makeQuery(id+"F15.opExtrude","SWEPT_BODY",BODY,{"disambiguationData":[OSD([sQuery(id+"F14.wireOp",EDGE,"E29.0.0"),sQuery(id+"F14.wireOp",EDGE,"E29.0.1"),sQuery(id+"F14.wireOp",EDGE,"E29.0.2"),sQuery(id+"F14.wireOp",EDGE,"E29.0.3")])]});
            deleteBodies(context, id + "F16", {"entities" : qUnion([Q0])});
        }
        {
            var Q0;
            Q0=makeQuery(id+"F3.opExtrude","SWEPT_FACE",FACE,{"disambiguationData":[OSD([sQuery(id+"F0.wireOp",EDGE,"E0.bottom")])]});
            var sketch = newSketch(context, id + "F17", { "sketchPlane" : qUnion([Q0])});
            skLineSegment(sketch, "E31", {"start": v(9, 199.33) * mm, "end": v(9, -300.67) * mm, "construction": true});
            skLineSegment(sketch, "E32", {"start": v(0, -50.67) * mm, "end": v(18, -50.67) * mm, "construction": true});
            skPoint(sketch, "E33", {"position": v(9, -50.67) * mm});
            skPoint(sketch, "E34", {"position": v(9, 169.33) * mm});
            skPoint(sketch, "E35.0.1.0", {"position": v(9, 129.33) * mm});
            skPoint(sketch, "E35.0.2.0", {"position": v(9, 89.33) * mm});
            skLineSegment(sketch, "E35.direction1", {"start": v(9, 169.33) * mm, "end": v(34, 169.33) * mm, "construction": true});
            skLineSegment(sketch, "E35.direction2", {"start": v(9, 169.33) * mm, "end": v(9, 129.33) * mm, "construction": true});
            skPoint(sketch, "E36.MirrorP", {"position": v(9, -270.67) * mm});
            skPoint(sketch, "E37.MirrorP", {"position": v(9, -230.67) * mm});
            skPoint(sketch, "E38.MirrorP", {"position": v(9, -190.67) * mm});
            skSolve(sketch);
        }
        {
            var Q0;
            Q0=sQuery(id+"F17.wireOp",VERTEX,"E34");
            var Q1;
            Q1=sQuery(id+"F17.wireOp",VERTEX,"E35.0.2.0");
            var Q2;
            Q2=sQuery(id+"F17.wireOp",VERTEX,"E38.MirrorP");
            var Q3;
            Q3=sQuery(id+"F17.wireOp",VERTEX,"E36.MirrorP");
            var Q4;
            Q4=makeQuery(id+"F3.opExtrude","SWEPT_BODY",BODY,{"disambiguationData":[OSD([sQuery(id+"F0.wireOp",EDGE,"E0.bottom"),sQuery(id+"F0.wireOp",EDGE,"E0.top"),sQuery(id+"F0.wireOp",EDGE,"E0.left"),sQuery(id+"F0.wireOp",EDGE,"E0.right")])]});
            hole(context, id + "F18", {"style" : HoleStyle.SIMPLE, "endStyle" : HoleEndStyle.BLIND, "holeDiameter" : 8 * mm, "holeDepth" : 20 * mm, "isTappedThrough" : true, "tappedDepth" : 12 * mm, "tapClearance" : 3, "startFromSketch" : true, "locations" : qUnion([Q0, Q1, Q2, Q3]), "scope" : qUnion([Q4])});
        }
        {
            var Q0;
            Q0=sQuery(id+"F17.wireOp",VERTEX,"E35.0.1.0");
            var Q1;
            Q1=sQuery(id+"F17.wireOp",VERTEX,"E37.MirrorP");
            var Q2;
            Q2=makeQuery(id+"F3.opExtrude","SWEPT_BODY",BODY,{"disambiguationData":[OSD([sQuery(id+"F0.wireOp",EDGE,"E0.bottom"),sQuery(id+"F0.wireOp",EDGE,"E0.top"),sQuery(id+"F0.wireOp",EDGE,"E0.left"),sQuery(id+"F0.wireOp",EDGE,"E0.right")])]});
            hole(context, id + "F19", {"style" : HoleStyle.SIMPLE, "endStyle" : HoleEndStyle.BLIND, "holeDiameter" : 5 * mm, "holeDepth" : 60 * mm, "isTappedThrough" : true, "tappedDepth" : 12 * mm, "tapClearance" : 3, "startFromSketch" : true, "locations" : qUnion([Q0, Q1]), "scope" : qUnion([Q2])});
        }
        {
            var Q0;
            Q0=makeQuery(id+"F8.opExtrude","SWEPT_FACE",FACE,{"disambiguationData":[OSD([sQuery(id+"F7.wireOp",EDGE,"E23.bottom")])]});
            var sketch = newSketch(context, id + "F20", { "sketchPlane" : qUnion([Q0])});
            skLineSegment(sketch, "E39", {"start": v(9, 979.33) * mm, "end": v(9, 299.33) * mm, "construction": true});
            skPoint(sketch, "E40", {"position": v(9, 359.33) * mm});
            skPoint(sketch, "E41", {"position": v(9, 409.33) * mm});
            skPoint(sketch, "E42", {"position": v(9, 489.33) * mm});
            skPoint(sketch, "E43", {"position": v(9, 639.33) * mm});
            skPoint(sketch, "E44", {"position": v(9, 569.33) * mm});
            skLineSegment(sketch, "E45", {"start": v(-174.96, 639.33) * mm, "end": v(192.1, 639.33) * mm, "construction": true});
            skPoint(sketch, "E46.MirrorP", {"position": v(9, 709.33) * mm});
            skPoint(sketch, "E47.MirrorP", {"position": v(9, 789.33) * mm});
            skPoint(sketch, "E48.MirrorP", {"position": v(9, 869.33) * mm});
            skPoint(sketch, "E49.MirrorP", {"position": v(9, 919.33) * mm});
            skSolve(sketch);
        }
        {
            var Q0;
            Q0=sQuery(id+"F20.wireOp",VERTEX,"E48.MirrorP");
            var Q1;
            Q1=sQuery(id+"F20.wireOp",VERTEX,"E43");
            var Q2;
            Q2=sQuery(id+"F20.wireOp",VERTEX,"E41");
            var Q3;
            Q3=makeQuery(id+"F8.opExtrude","SWEPT_BODY",BODY,{"disambiguationData":[OSD([sQuery(id+"F7.wireOp",EDGE,"E23.bottom"),sQuery(id+"F7.wireOp",EDGE,"E23.top"),sQuery(id+"F7.wireOp",EDGE,"E23.left"),sQuery(id+"F7.wireOp",EDGE,"E23.right")])]});
            hole(context, id + "F21", {"style" : HoleStyle.SIMPLE, "endStyle" : HoleEndStyle.BLIND, "holeDiameter" : 4 * mm, "holeDepth" : 40 * mm, "isTappedThrough" : true, "tappedDepth" : 12 * mm, "tapClearance" : 3, "locations" : qUnion([Q0, Q1, Q2]), "scope" : qUnion([Q3])});
        }
        {
            var Q0;
            Q0=sQuery(id+"F20.wireOp",VERTEX,"E40");
            var Q1;
            Q1=sQuery(id+"F20.wireOp",VERTEX,"E42");
            var Q2;
            Q2=sQuery(id+"F20.wireOp",VERTEX,"E44");
            var Q3;
            Q3=sQuery(id+"F20.wireOp",VERTEX,"E46.MirrorP");
            var Q4;
            Q4=sQuery(id+"F20.wireOp",VERTEX,"E47.MirrorP");
            var Q5;
            Q5=sQuery(id+"F20.wireOp",VERTEX,"E49.MirrorP");
            var Q6;
            Q6=makeQuery(id+"F8.opExtrude","SWEPT_BODY",BODY,{"disambiguationData":[OSD([sQuery(id+"F7.wireOp",EDGE,"E23.bottom"),sQuery(id+"F7.wireOp",EDGE,"E23.top"),sQuery(id+"F7.wireOp",EDGE,"E23.left"),sQuery(id+"F7.wireOp",EDGE,"E23.right")])]});
            hole(context, id + "F22", {"style" : HoleStyle.SIMPLE, "endStyle" : HoleEndStyle.BLIND, "holeDiameter" : 8 * mm, "holeDepth" : 30 * mm, "isTappedThrough" : true, "tappedDepth" : 12 * mm, "tapClearance" : 3, "locations" : qUnion([Q0, Q1, Q2, Q3, Q4, Q5]), "scope" : qUnion([Q6])});
        }
        {
            var Q0;
            Q0=makeQuery(id+"F3.opExtrude","SWEPT_FACE",FACE,{"disambiguationData":[OSD([sQuery(id+"F0.wireOp",EDGE,"E0.left")])]});
            cPlane(context, id + "F23", {"entities" : qUnion([Q0]), "cplaneType" : CPlaneType.OFFSET, "offset" : 25 * mm, "width" : 150 * mm, "height" : 150 * mm});
        }
        {
            var Q0;
            Q0=qCreatedBy(makeId("Front.planeOp"),FACE);
            var sketch = newSketch(context, id + "F24", { "sketchPlane" : qUnion([Q0])});
            skLineSegment(sketch, "E50.bottom", {"start": v(-2076.4, -778.8) * mm, "end": v(-506.4, -778.8) * mm});
            skLineSegment(sketch, "E50.top", {"start": v(-2076.4, -808.8) * mm, "end": v(-506.4, -808.8) * mm});
            skLineSegment(sketch, "E50.left", {"start": v(-2076.4, -778.8) * mm, "end": v(-2076.4, -808.8) * mm});
            skLineSegment(sketch, "E50.right", {"start": v(-506.4, -778.8) * mm, "end": v(-506.4, -808.8) * mm});
            skSolve(sketch);
        }
        {
            var Q0;
            Q0=qSketchRegion(id+"F24",true);
            extrude(context, id + "F25", {"entities" : qUnion([Q0]), "depth" : 18 * mm});
        }
        {
            var Q0;
            Q0=makeQuery(id+"F25.opExtrude","CAP_FACE",FACE,{"disambiguationData":[OSD([sQuery(id+"F24.wireOp",EDGE,"E50.bottom"),sQuery(id+"F24.wireOp",EDGE,"E50.top"),sQuery(id+"F24.wireOp",EDGE,"E50.left"),sQuery(id+"F24.wireOp",EDGE,"E50.right")])],"isStart":true});
            var sketch = newSketch(context, id + "F26", { "sketchPlane" : qUnion([Q0])});
            skLineSegment(sketch, "E51", {"start": v(2067.4, -778.8) * mm, "end": v(2067.4, -808.8) * mm, "construction": true});
            skPoint(sketch, "E52", {"position": v(2067.4, -787.8) * mm});
            skPoint(sketch, "E53", {"position": v(2067.4, -801.3) * mm});
            skLineSegment(sketch, "E54", {"start": v(1291.4, -778.8) * mm, "end": v(1291.4, -808.8) * mm, "construction": true});
            skPoint(sketch, "E55.MirrorP", {"position": v(515.4, -787.8) * mm});
            skPoint(sketch, "E56.MirrorP", {"position": v(515.4, -801.3) * mm});
            skSolve(sketch);
        }
        {
            var Q0;
            Q0=sQuery(id+"F26.wireOp",VERTEX,"E52");
            var Q1;
            Q1=sQuery(id+"F26.wireOp",VERTEX,"E55.MirrorP");
            var Q2;
            Q2=makeQuery(id+"F25.opExtrude","SWEPT_BODY",BODY,{"disambiguationData":[OSD([sQuery(id+"F24.wireOp",EDGE,"E50.bottom"),sQuery(id+"F24.wireOp",EDGE,"E50.top"),sQuery(id+"F24.wireOp",EDGE,"E50.left"),sQuery(id+"F24.wireOp",EDGE,"E50.right")])]});
            hole(context, id + "F27", {"style" : HoleStyle.SIMPLE, "endStyle" : HoleEndStyle.BLIND, "holeDiameter" : 8 * mm, "holeDepth" : 10 * mm, "isTappedThrough" : true, "tappedDepth" : 12 * mm, "tapClearance" : 3, "locations" : qUnion([Q0, Q1]), "scope" : qUnion([Q2])});
        }
        {
            var Q0;
            Q0=sQuery(id+"F26.wireOp",VERTEX,"E56.MirrorP");
            var Q1;
            Q1=sQuery(id+"F26.wireOp",VERTEX,"E53");
            var Q2;
            Q2=makeQuery(id+"F25.opExtrude","SWEPT_BODY",BODY,{"disambiguationData":[OSD([sQuery(id+"F24.wireOp",EDGE,"E50.bottom"),sQuery(id+"F24.wireOp",EDGE,"E50.top"),sQuery(id+"F24.wireOp",EDGE,"E50.left"),sQuery(id+"F24.wireOp",EDGE,"E50.right")])]});
            hole(context, id + "F28", {"style" : HoleStyle.SIMPLE, "endStyle" : HoleEndStyle.BLIND, "holeDiameter" : 4 * mm, "holeDepth" : 10 * mm, "isTappedThrough" : true, "tappedDepth" : 12 * mm, "tapClearance" : 3, "locations" : qUnion([Q0, Q1]), "scope" : qUnion([Q2])});
        }
        {
            var Q0;
            Q0=qCreatedBy(makeId("Front.planeOp"),FACE);
            var sketch = newSketch(context, id + "F29", { "sketchPlane" : qUnion([Q0])});
            skLineSegment(sketch, "E57.bottom", {"start": v(0, -861.57) * mm, "end": v(-1380, -861.57) * mm});
            skLineSegment(sketch, "E57.top", {"start": v(0, -891.57) * mm, "end": v(-1380, -891.57) * mm});
            skLineSegment(sketch, "E57.left", {"start": v(0, -861.57) * mm, "end": v(0, -891.57) * mm});
            skLineSegment(sketch, "E57.right", {"start": v(-1380, -861.57) * mm, "end": v(-1380, -891.57) * mm});
            skSolve(sketch);
        }
        {
            var Q0;
            Q0=qSketchRegion(id+"F29",true);
            extrude(context, id + "F30", {"entities" : qUnion([Q0]), "depth" : 18 * mm});
        }
        {
            var Q0;
            Q0=makeQuery(id+"F30.opExtrude","CAP_FACE",FACE,{"disambiguationData":[OSD([sQuery(id+"F29.wireOp",EDGE,"E57.bottom"),sQuery(id+"F29.wireOp",EDGE,"E57.top"),sQuery(id+"F29.wireOp",EDGE,"E57.left"),sQuery(id+"F29.wireOp",EDGE,"E57.right")])],"isStart":true});
            var sketch = newSketch(context, id + "F31", { "sketchPlane" : qUnion([Q0])});
            skLineSegment(sketch, "E58", {"start": v(1371, -861.57) * mm, "end": v(1371, -891.57) * mm, "construction": true});
            skPoint(sketch, "E59", {"position": v(1371, -870.57) * mm});
            skPoint(sketch, "E60", {"position": v(1371, -884.07) * mm});
            skLineSegment(sketch, "E61", {"start": v(690, -861.57) * mm, "end": v(690, -891.57) * mm, "construction": true});
            skPoint(sketch, "E62.MirrorP", {"position": v(9, -870.57) * mm});
            skPoint(sketch, "E63.MirrorP", {"position": v(9, -884.07) * mm});
            skSolve(sketch);
        }
        {
            var Q0;
            Q0=sQuery(id+"F31.wireOp",VERTEX,"E63.MirrorP");
            var Q1;
            Q1=sQuery(id+"F31.wireOp",VERTEX,"E60");
            var Q2;
            Q2=makeQuery(id+"F30.opExtrude","SWEPT_BODY",BODY,{"disambiguationData":[OSD([sQuery(id+"F29.wireOp",EDGE,"E57.bottom"),sQuery(id+"F29.wireOp",EDGE,"E57.top"),sQuery(id+"F29.wireOp",EDGE,"E57.left"),sQuery(id+"F29.wireOp",EDGE,"E57.right")])]});
            hole(context, id + "F32", {"style" : HoleStyle.SIMPLE, "endStyle" : HoleEndStyle.BLIND, "holeDiameter" : 4 * mm, "holeDepth" : 10 * mm, "isTappedThrough" : true, "tappedDepth" : 12 * mm, "tapClearance" : 3, "locations" : qUnion([Q0, Q1]), "scope" : qUnion([Q2])});
        }
        {
            var Q0;
            Q0=sQuery(id+"F31.wireOp",VERTEX,"E62.MirrorP");
            var Q1;
            Q1=sQuery(id+"F31.wireOp",VERTEX,"E59");
            var Q2;
            Q2=makeQuery(id+"F30.opExtrude","SWEPT_BODY",BODY,{"disambiguationData":[OSD([sQuery(id+"F29.wireOp",EDGE,"E57.bottom"),sQuery(id+"F29.wireOp",EDGE,"E57.top"),sQuery(id+"F29.wireOp",EDGE,"E57.left"),sQuery(id+"F29.wireOp",EDGE,"E57.right")])]});
            hole(context, id + "F33", {"style" : HoleStyle.SIMPLE, "endStyle" : HoleEndStyle.BLIND, "holeDiameter" : 8 * mm, "holeDepth" : 10 * mm, "isTappedThrough" : true, "tappedDepth" : 12 * mm, "tapClearance" : 3, "locations" : qUnion([Q0, Q1]), "scope" : qUnion([Q2])});
        }
        {
            var Q0;
            Q0=makeQuery(id+"F3.opExtrude","SWEPT_FACE",FACE,{"disambiguationData":[OSD([sQuery(id+"F0.wireOp",EDGE,"E0.left")])]});
            var sketch = newSketch(context, id + "F34", { "sketchPlane" : qUnion([Q0])});
            skLineSegment(sketch, "E64.bottom", {"start": v(0, 487.5) * mm, "end": v(18, 487.5) * mm});
            skLineSegment(sketch, "E64.top", {"start": v(0, -312.5) * mm, "end": v(18, -312.5) * mm});
            skLineSegment(sketch, "E64.left", {"start": v(18, 487.5) * mm, "end": v(18, -312.5) * mm});
            skLineSegment(sketch, "E64.right", {"start": v(0, 487.5) * mm, "end": v(0, -312.5) * mm});
            skLineSegment(sketch, "E65.bottom", {"start": v(0, 407.5) * mm, "end": v(18, 407.5) * mm, "construction": true});
            skLineSegment(sketch, "E65.top", {"start": v(0, 127.5) * mm, "end": v(18, 127.5) * mm, "construction": true});
            skLineSegment(sketch, "E65.left", {"start": v(18, 407.5) * mm, "end": v(18, 127.5) * mm, "construction": true});
            skLineSegment(sketch, "E65.right", {"start": v(0, 407.5) * mm, "end": v(0, 127.5) * mm, "construction": true});
            skLineSegment(sketch, "E66.bottom", {"start": v(0, -212.5) * mm, "end": v(18, -212.5) * mm, "construction": true});
            skLineSegment(sketch, "E66.top", {"start": v(0, 67.5) * mm, "end": v(18, 67.5) * mm, "construction": true});
            skLineSegment(sketch, "E66.left", {"start": v(18, -212.5) * mm, "end": v(18, 67.5) * mm, "construction": true});
            skLineSegment(sketch, "E66.right", {"start": v(0, -212.5) * mm, "end": v(0, 67.5) * mm, "construction": true});
            skLineSegment(sketch, "E67", {"start": v(9, 67.5) * mm, "end": v(9, -212.5) * mm, "construction": true});
            skPoint(sketch, "E68", {"position": v(9, 37.5) * mm});
            skPoint(sketch, "E69", {"position": v(9, -2.5) * mm});
            skPoint(sketch, "E70", {"position": v(9, -72.5) * mm});
            skPoint(sketch, "E71", {"position": v(9, -142.5) * mm});
            skPoint(sketch, "E72", {"position": v(9, -182.5) * mm});
            skLineSegment(sketch, "E73", {"start": v(9, 407.5) * mm, "end": v(9, 127.5) * mm, "construction": true});
            skPoint(sketch, "E74", {"position": v(9, 377.5) * mm});
            skPoint(sketch, "E75", {"position": v(9, 337.5) * mm});
            skPoint(sketch, "E76", {"position": v(9, 267.5) * mm});
            skPoint(sketch, "E77", {"position": v(9, 197.5) * mm});
            skPoint(sketch, "E78", {"position": v(9, 157.5) * mm});
            skSolve(sketch);
        }
        {
            var Q0;
            Q0=sQuery(id+"F34.wireOp",VERTEX,"E74");
            var Q1;
            Q1=sQuery(id+"F34.wireOp",VERTEX,"E76");
            var Q2;
            Q2=sQuery(id+"F34.wireOp",VERTEX,"E78");
            var Q3;
            Q3=sQuery(id+"F34.wireOp",VERTEX,"E72");
            var Q4;
            Q4=sQuery(id+"F34.wireOp",VERTEX,"E70");
            var Q5;
            Q5=sQuery(id+"F34.wireOp",VERTEX,"E68");
            var Q6;
            Q6=makeQuery(id+"F3.opExtrude","SWEPT_BODY",BODY,{"disambiguationData":[OSD([sQuery(id+"F0.wireOp",EDGE,"E0.bottom"),sQuery(id+"F0.wireOp",EDGE,"E0.top"),sQuery(id+"F0.wireOp",EDGE,"E0.left"),sQuery(id+"F0.wireOp",EDGE,"E0.right")])]});
            hole(context, id + "F35", {"style" : HoleStyle.SIMPLE, "endStyle" : HoleEndStyle.BLIND, "holeDiameter" : 8 * mm, "holeDepth" : 20 * mm, "isTappedThrough" : true, "tappedDepth" : 12 * mm, "tapClearance" : 3, "locations" : qUnion([Q0, Q1, Q2, Q3, Q4, Q5]), "scope" : qUnion([Q6])});
        }
        {
            var Q0;
            Q0=sQuery(id+"F34.wireOp",VERTEX,"E75");
            var Q1;
            Q1=sQuery(id+"F34.wireOp",VERTEX,"E77");
            var Q2;
            Q2=sQuery(id+"F34.wireOp",VERTEX,"E69");
            var Q3;
            Q3=sQuery(id+"F34.wireOp",VERTEX,"E71");
            var Q4;
            Q4=makeQuery(id+"F3.opExtrude","SWEPT_BODY",BODY,{"disambiguationData":[OSD([sQuery(id+"F0.wireOp",EDGE,"E0.bottom"),sQuery(id+"F0.wireOp",EDGE,"E0.top"),sQuery(id+"F0.wireOp",EDGE,"E0.left"),sQuery(id+"F0.wireOp",EDGE,"E0.right")])]});
            hole(context, id + "F36", {"style" : HoleStyle.SIMPLE, "endStyle" : HoleEndStyle.BLIND, "holeDiameter" : 4 * mm, "holeDepth" : 40 * mm, "isTappedThrough" : true, "tappedDepth" : 12 * mm, "tapClearance" : 3, "locations" : qUnion([Q0, Q1, Q2, Q3]), "scope" : qUnion([Q4])});
        }
        {
            var Q0;
            Q0=makeQuery(id+"F3.opExtrude","SWEPT_FACE",FACE,{"disambiguationData":[OSD([sQuery(id+"F0.wireOp",EDGE,"E0.right")])]});
            var sketch = newSketch(context, id + "F37", { "sketchPlane" : qUnion([Q0])});
            skLineSegment(sketch, "E79", {"start": v(-9, 487.5) * mm, "end": v(-9, 442.5) * mm, "construction": true});
            skPoint(sketch, "E80", {"position": v(-9, 478.5) * mm});
            skPoint(sketch, "E81", {"position": v(-9, 465) * mm});
            skSolve(sketch);
        }
        {
            var Q0;
            Q0=sQuery(id+"F37.wireOp",VERTEX,"E80");
            var Q1;
            Q1=makeQuery(id+"F3.opExtrude","SWEPT_BODY",BODY,{"disambiguationData":[OSD([sQuery(id+"F0.wireOp",EDGE,"E0.bottom"),sQuery(id+"F0.wireOp",EDGE,"E0.top"),sQuery(id+"F0.wireOp",EDGE,"E0.left"),sQuery(id+"F0.wireOp",EDGE,"E0.right")])]});
            hole(context, id + "F38", {"style" : HoleStyle.SIMPLE, "endStyle" : HoleEndStyle.THROUGH, "holeDiameter" : 8 * mm, "isTappedThrough" : true, "tappedDepth" : 12 * mm, "tapClearance" : 3, "locations" : qUnion([Q0]), "scope" : qUnion([Q1])});
        }
        {
            var Q0;
            Q0=sQuery(id+"F37.wireOp",VERTEX,"E81");
            var Q1;
            Q1=makeQuery(id+"F3.opExtrude","SWEPT_BODY",BODY,{"disambiguationData":[OSD([sQuery(id+"F0.wireOp",EDGE,"E0.bottom"),sQuery(id+"F0.wireOp",EDGE,"E0.top"),sQuery(id+"F0.wireOp",EDGE,"E0.left"),sQuery(id+"F0.wireOp",EDGE,"E0.right")])]});
            hole(context, id + "F39", {"style" : HoleStyle.SIMPLE, "endStyle" : HoleEndStyle.THROUGH, "holeDiameter" : 4 * mm, "isTappedThrough" : true, "tappedDepth" : 12 * mm, "tapClearance" : 3, "locations" : qUnion([Q0]), "scope" : qUnion([Q1])});
        }
        {
            var Q0;
            Q0=makeQuery(id+"F3.opExtrude","SWEPT_BODY",BODY,{"disambiguationData":[OSD([sQuery(id+"F0.wireOp",EDGE,"E0.bottom"),sQuery(id+"F0.wireOp",EDGE,"E0.top"),sQuery(id+"F0.wireOp",EDGE,"E0.left"),sQuery(id+"F0.wireOp",EDGE,"E0.right")])]});
            var Q1;
            Q1=qCreatedBy(id+"F23.planeOp",FACE);
            mirror(context, id + "F40", {"entities" : qUnion([Q0]), "mirrorPlane" : qUnion([Q1])});
        }
        {
            var Q0;
            Q0=sQuery(id+"F34.wireOp",VERTEX,"E75");
            var Q1;
            Q1=sQuery(id+"F34.wireOp",VERTEX,"E77");
            var Q2;
            Q2=sQuery(id+"F34.wireOp",VERTEX,"E69");
            var Q3;
            Q3=sQuery(id+"F34.wireOp",VERTEX,"E71");
            var Q4;
            Q4=makeQuery(id+"F8.opExtrude","SWEPT_BODY",BODY,{"disambiguationData":[OSD([sQuery(id+"F7.wireOp",EDGE,"E23.bottom"),sQuery(id+"F7.wireOp",EDGE,"E23.top"),sQuery(id+"F7.wireOp",EDGE,"E23.left"),sQuery(id+"F7.wireOp",EDGE,"E23.right")])]});
            hole(context, id + "F41", {"style" : HoleStyle.SIMPLE, "endStyle" : HoleEndStyle.BLIND, "holeDiameter" : 4 * mm, "holeDepth" : 40 * mm, "isTappedThrough" : true, "tappedDepth" : 12 * mm, "tapClearance" : 3, "locations" : qUnion([Q0, Q1, Q2, Q3]), "scope" : qUnion([Q4])});
        }
        {
            var Q0;
            Q0=sQuery(id+"F34.wireOp",VERTEX,"E74");
            var Q1;
            Q1=sQuery(id+"F34.wireOp",VERTEX,"E76");
            var Q2;
            Q2=sQuery(id+"F34.wireOp",VERTEX,"E78");
            var Q3;
            Q3=sQuery(id+"F34.wireOp",VERTEX,"E68");
            var Q4;
            Q4=sQuery(id+"F34.wireOp",VERTEX,"E70");
            var Q5;
            Q5=sQuery(id+"F34.wireOp",VERTEX,"E72");
            var Q6;
            Q6=makeQuery(id+"F8.opExtrude","SWEPT_BODY",BODY,{"disambiguationData":[OSD([sQuery(id+"F7.wireOp",EDGE,"E23.bottom"),sQuery(id+"F7.wireOp",EDGE,"E23.top"),sQuery(id+"F7.wireOp",EDGE,"E23.left"),sQuery(id+"F7.wireOp",EDGE,"E23.right")])]});
            hole(context, id + "F42", {"style" : HoleStyle.SIMPLE, "endStyle" : HoleEndStyle.BLIND, "holeDiameter" : 8 * mm, "holeDepth" : 25 * mm, "isTappedThrough" : true, "tappedDepth" : 12 * mm, "tapClearance" : 3, "locations" : qUnion([Q0, Q1, Q2, Q3, Q4, Q5]), "scope" : qUnion([Q6])});
        }
        {
            var Q0;
            Q0=makeQuery(id+"F8.opExtrude","SWEPT_BODY",BODY,{"disambiguationData":[OSD([sQuery(id+"F7.wireOp",EDGE,"E23.bottom"),sQuery(id+"F7.wireOp",EDGE,"E23.top"),sQuery(id+"F7.wireOp",EDGE,"E23.left"),sQuery(id+"F7.wireOp",EDGE,"E23.right")])]});
            var Q1;
            Q1=qCreatedBy(id+"F23.planeOp",FACE);
            mirror(context, id + "F43", {"entities" : qUnion([Q0]), "mirrorPlane" : qUnion([Q1])});
        }
        {
            var Q0;
            Q0=makeQuery(id+"F15.opExtrude","CAP_FACE",FACE,{"disambiguationData":[OSD([sQuery(id+"F14.wireOp",EDGE,"E30.bottom"),sQuery(id+"F14.wireOp",EDGE,"E30.top"),sQuery(id+"F14.wireOp",EDGE,"E30.left"),sQuery(id+"F14.wireOp",EDGE,"E30.right")])],"isStart":true});
            var sketch = newSketch(context, id + "F44", { "sketchPlane" : qUnion([Q0])});
            skLineSegment(sketch, "E82.bottom", {"start": v(933.53, 83.9) * mm, "end": v(951.53, 83.9) * mm, "construction": true});
            skLineSegment(sketch, "E82.top", {"start": v(933.53, -196.1) * mm, "end": v(951.53, -196.1) * mm, "construction": true});
            skLineSegment(sketch, "E82.left", {"start": v(933.53, 83.9) * mm, "end": v(933.53, -196.1) * mm, "construction": true});
            skLineSegment(sketch, "E82.right", {"start": v(951.53, 83.9) * mm, "end": v(951.53, -196.1) * mm, "construction": true});
            skLineSegment(sketch, "E83.bottom", {"start": v(898.9, -688.71) * mm, "end": v(916.9, -688.71) * mm, "construction": true});
            skLineSegment(sketch, "E83.top", {"start": v(898.9, -408.71) * mm, "end": v(916.9, -408.71) * mm, "construction": true});
            skLineSegment(sketch, "E83.left", {"start": v(898.9, -688.71) * mm, "end": v(898.9, -408.71) * mm, "construction": true});
            skLineSegment(sketch, "E83.right", {"start": v(916.9, -688.71) * mm, "end": v(916.9, -408.71) * mm, "construction": true});
            skLineSegment(sketch, "E84", {"start": v(907.9, -408.71) * mm, "end": v(907.9, -688.71) * mm, "construction": true});
            skPoint(sketch, "E85", {"position": v(907.9, -438.71) * mm});
            skPoint(sketch, "E86", {"position": v(907.9, -478.71) * mm});
            skPoint(sketch, "E87", {"position": v(907.9, -548.71) * mm});
            skPoint(sketch, "E88", {"position": v(907.9, -618.71) * mm});
            skPoint(sketch, "E89", {"position": v(907.9, -658.71) * mm});
            skLineSegment(sketch, "E90", {"start": v(942.53, 83.9) * mm, "end": v(942.53, -196.1) * mm, "construction": true});
            skPoint(sketch, "E91", {"position": v(942.53, 53.9) * mm});
            skPoint(sketch, "E92", {"position": v(942.53, 13.9) * mm});
            skPoint(sketch, "E93", {"position": v(942.53, -56.1) * mm});
            skPoint(sketch, "E94", {"position": v(942.53, -126.1) * mm});
            skPoint(sketch, "E95", {"position": v(942.53, -166.1) * mm});
            skLineSegment(sketch, "E96", {"start": v(131.9, -408.71) * mm, "end": v(131.9, -688.71) * mm, "construction": true});
            skLineSegment(sketch, "E97.MirrorCS", {"start": v(-635.1, -688.71) * mm, "end": v(-653.1, -688.71) * mm, "construction": true});
            skLineSegment(sketch, "E98.MirrorCS", {"start": v(-635.1, -408.71) * mm, "end": v(-653.1, -408.71) * mm, "construction": true});
            skLineSegment(sketch, "E99.MirrorCS", {"start": v(-635.1, -688.71) * mm, "end": v(-635.1, -408.71) * mm, "construction": true});
            skPoint(sketch, "E100.MirrorP", {"position": v(-644.1, -438.71) * mm});
            skLineSegment(sketch, "E101.MirrorCS", {"start": v(-653.1, -688.71) * mm, "end": v(-653.1, -408.71) * mm, "construction": true});
            skPoint(sketch, "E102.MirrorP", {"position": v(-644.1, -548.71) * mm});
            skPoint(sketch, "E103.MirrorP", {"position": v(-644.1, -618.71) * mm});
            skPoint(sketch, "E104.MirrorP", {"position": v(-644.1, -478.71) * mm});
            skLineSegment(sketch, "E105.MirrorCS", {"start": v(-644.1, -408.71) * mm, "end": v(-644.1, -688.71) * mm, "construction": true});
            skPoint(sketch, "E106.MirrorP", {"position": v(-644.1, -658.71) * mm});
            skLineSegment(sketch, "E107", {"start": v(261.53, 83.9) * mm, "end": v(261.53, -196.1) * mm, "construction": true});
            skLineSegment(sketch, "E108.MirrorCS", {"start": v(-410.47, -196.1) * mm, "end": v(-428.47, -196.1) * mm, "construction": true});
            skLineSegment(sketch, "E109.MirrorCS", {"start": v(-410.47, 83.9) * mm, "end": v(-428.47, 83.9) * mm, "construction": true});
            skPoint(sketch, "E110.MirrorP", {"position": v(-419.47, -166.1) * mm});
            skPoint(sketch, "E111.MirrorP", {"position": v(-419.47, 13.9) * mm});
            skPoint(sketch, "E112.MirrorP", {"position": v(-419.47, -126.1) * mm});
            skLineSegment(sketch, "E113.MirrorCS", {"start": v(-419.47, 83.9) * mm, "end": v(-419.47, -196.1) * mm, "construction": true});
            skPoint(sketch, "E114.MirrorP", {"position": v(-419.47, -56.1) * mm});
            skPoint(sketch, "E115.MirrorP", {"position": v(-419.47, 53.9) * mm});
            skLineSegment(sketch, "E116.MirrorCS", {"start": v(-410.47, 83.9) * mm, "end": v(-410.47, -196.1) * mm, "construction": true});
            skLineSegment(sketch, "E117.MirrorCS", {"start": v(-428.47, 83.9) * mm, "end": v(-428.47, -196.1) * mm, "construction": true});
            skSolve(sketch);
        }
        {
            var Q0;
            Q0=sQuery(id+"F44.wireOp",VERTEX,"E115.MirrorP");
            var Q1;
            Q1=sQuery(id+"F44.wireOp",VERTEX,"E114.MirrorP");
            var Q2;
            Q2=sQuery(id+"F44.wireOp",VERTEX,"E110.MirrorP");
            var Q3;
            Q3=sQuery(id+"F44.wireOp",VERTEX,"E95");
            var Q4;
            Q4=sQuery(id+"F44.wireOp",VERTEX,"E93");
            var Q5;
            Q5=sQuery(id+"F44.wireOp",VERTEX,"E91");
            var Q6;
            Q6=makeQuery(id+"F15.opExtrude","SWEPT_BODY",BODY,{"disambiguationData":[OSD([sQuery(id+"F14.wireOp",EDGE,"E30.bottom"),sQuery(id+"F14.wireOp",EDGE,"E30.top"),sQuery(id+"F14.wireOp",EDGE,"E30.left"),sQuery(id+"F14.wireOp",EDGE,"E30.right")])]});
            hole(context, id + "F45", {"style" : HoleStyle.SIMPLE, "endStyle" : HoleEndStyle.BLIND, "holeDiameter" : 8 * mm, "holeDepth" : 10 * mm, "isTappedThrough" : true, "tappedDepth" : 12 * mm, "tapClearance" : 3, "locations" : qUnion([Q0, Q1, Q2, Q3, Q4, Q5]), "scope" : qUnion([Q6])});
        }
        {
            var Q0;
            Q0=sQuery(id+"F44.wireOp",VERTEX,"E100.MirrorP");
            var Q1;
            Q1=sQuery(id+"F44.wireOp",VERTEX,"E102.MirrorP");
            var Q2;
            Q2=sQuery(id+"F44.wireOp",VERTEX,"E106.MirrorP");
            var Q3;
            Q3=sQuery(id+"F44.wireOp",VERTEX,"E85");
            var Q4;
            Q4=sQuery(id+"F44.wireOp",VERTEX,"E87");
            var Q5;
            Q5=sQuery(id+"F44.wireOp",VERTEX,"E89");
            var Q6;
            Q6=makeQuery(id+"F13.opExtrude","SWEPT_BODY",BODY,{"disambiguationData":[OSD([sQuery(id+"F12.wireOp",EDGE,"E28.bottom"),sQuery(id+"F12.wireOp",EDGE,"E28.top"),sQuery(id+"F12.wireOp",EDGE,"E28.left"),sQuery(id+"F12.wireOp",EDGE,"E28.right")])]});
            hole(context, id + "F46", {"style" : HoleStyle.SIMPLE, "endStyle" : HoleEndStyle.BLIND, "holeDiameter" : 8 * mm, "holeDepth" : 10 * mm, "isTappedThrough" : true, "tappedDepth" : 12 * mm, "tapClearance" : 3, "locations" : qUnion([Q0, Q1, Q2, Q3, Q4, Q5]), "scope" : qUnion([Q6])});
        }
        {
            var Q0;
            Q0=sQuery(id+"F44.wireOp",VERTEX,"E104.MirrorP");
            var Q1;
            Q1=sQuery(id+"F44.wireOp",VERTEX,"E103.MirrorP");
            var Q2;
            Q2=sQuery(id+"F44.wireOp",VERTEX,"E88");
            var Q3;
            Q3=sQuery(id+"F44.wireOp",VERTEX,"E86");
            var Q4;
            Q4=makeQuery(id+"F13.opExtrude","SWEPT_BODY",BODY,{"disambiguationData":[OSD([sQuery(id+"F12.wireOp",EDGE,"E28.bottom"),sQuery(id+"F12.wireOp",EDGE,"E28.top"),sQuery(id+"F12.wireOp",EDGE,"E28.left"),sQuery(id+"F12.wireOp",EDGE,"E28.right")])]});
            hole(context, id + "F47", {"style" : HoleStyle.SIMPLE, "endStyle" : HoleEndStyle.BLIND, "holeDiameter" : 4 * mm, "holeDepth" : 12 * mm, "isTappedThrough" : true, "tappedDepth" : 12 * mm, "tapClearance" : 3, "locations" : qUnion([Q0, Q1, Q2, Q3]), "scope" : qUnion([Q4])});
        }
        {
            var Q0;
            Q0=sQuery(id+"F44.wireOp",VERTEX,"E111.MirrorP");
            var Q1;
            Q1=sQuery(id+"F44.wireOp",VERTEX,"E112.MirrorP");
            var Q2;
            Q2=sQuery(id+"F44.wireOp",VERTEX,"E94");
            var Q3;
            Q3=sQuery(id+"F44.wireOp",VERTEX,"E92");
            var Q4;
            Q4=makeQuery(id+"F15.opExtrude","SWEPT_BODY",BODY,{"disambiguationData":[OSD([sQuery(id+"F14.wireOp",EDGE,"E30.bottom"),sQuery(id+"F14.wireOp",EDGE,"E30.top"),sQuery(id+"F14.wireOp",EDGE,"E30.left"),sQuery(id+"F14.wireOp",EDGE,"E30.right")])]});
            hole(context, id + "F48", {"style" : HoleStyle.SIMPLE, "endStyle" : HoleEndStyle.BLIND, "holeDiameter" : 4 * mm, "holeDepth" : 12 * mm, "isTappedThrough" : true, "tappedDepth" : 12 * mm, "tapClearance" : 3, "locations" : qUnion([Q0, Q1, Q2, Q3]), "scope" : qUnion([Q4])});
        }
        {
            var Q0;
            Q0=makeQuery(id+"F15.opExtrude","SWEPT_BODY",BODY,{"disambiguationData":[OSD([sQuery(id+"F14.wireOp",EDGE,"E30.bottom"),sQuery(id+"F14.wireOp",EDGE,"E30.top"),sQuery(id+"F14.wireOp",EDGE,"E30.left"),sQuery(id+"F14.wireOp",EDGE,"E30.right")])]});
            transform(context, id + "F49", {"entities" : qUnion([Q0]), "transformType" : TransformType.TRANSLATION_3D, "dx" : 0 * mm, "dy" : 0 * mm, "dz" : 700 * mm, "makeCopy" : true});
        }
    });
